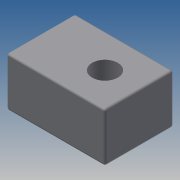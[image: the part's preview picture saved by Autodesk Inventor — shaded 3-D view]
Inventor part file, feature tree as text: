
AUTODESK INVENTOR PART (.ipt)
format: ipt  version: 2013 (Build 170138000, 138)  size: 94,208 bytes
history: native  units: mm
features: extrude x1, fillet x1, sketch x1
ambient origin geometry x8: Origin, YZ Plane, XZ Plane, XY Plane, X Axis, Y Axis, Z Axis, Center Point
bodies: Solid1 (feature_tree)
feature tree (3):
  extrude  "Extrusion1"  Depth=16.0mm
  fillet  "Fillet1"  Radius=6.0mm
  sketch  "Sketch1"  dims[d0=23.0mm d2=16.0mm d3=6.0mm d4=8.0mm d5=11.5mm d6=0.0mm d7=0.5mm]
